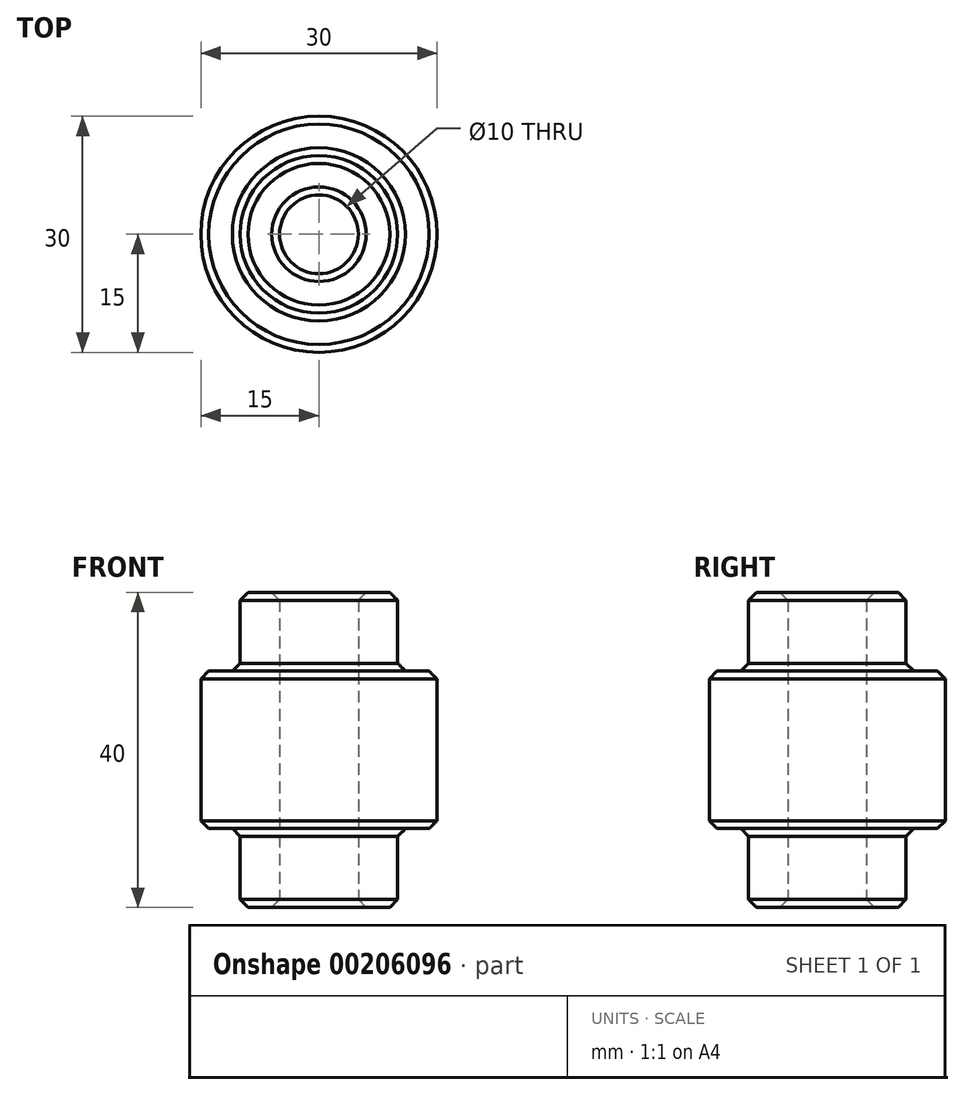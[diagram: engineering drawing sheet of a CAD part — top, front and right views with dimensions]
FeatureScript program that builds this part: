
annotation { "Feature Type Name" : "Feature", "Feature Type Description" : "" }
export const myFeature = defineFeature(function(context is Context, id is Id, definition is map)
    precondition{}
    {
        {
            var Q0;
            Q0=qCreatedBy(makeId("Top.planeOp"),FACE);
            var sketch = newSketch(context, id + "F0", { "sketchPlane" : qUnion([Q0])});
            skCircle(sketch, "E0", {"center": v(0, 0) * mm, "radius": 15 * mm});
            skSolve(sketch);
        }
        {
            var Q0;
            Q0=makeQuery(id+"F0.imprint","IMPRINT",FACE,{"disambiguationData":[TD([[makeQuery(id+"F0.imprint","IMPRINT",EDGE,{"derivedFrom":sQuery(id+"F0.wireOp",EDGE,"E0")}),1.0]])]});
            extrude(context, id + "F1", {"entities" : qUnion([Q0]), "depth" : 10 * mm, "hasSecondDirection" : true, "secondDirectionOppositeDirection" : true, "secondDirectionDepth" : 10 * mm});
        }
        {
            var Q0;
            Q0=makeQuery(id+"F1.opExtrude","CAP_FACE",FACE,{"disambiguationData":[OSD([sQuery(id+"F0.wireOp",EDGE,"E0")])],"isStart":false});
            var sketch = newSketch(context, id + "F2", { "sketchPlane" : qUnion([Q0])});
            skCircle(sketch, "E1", {"center": v(0, 0) * mm, "radius": 10 * mm});
            skSolve(sketch);
        }
        {
            var Q0;
            Q0 = qSketchRegion(id + "F2", true);
            extrude(context, id + "F3", {"entities" : qUnion([Q0]), "operationType" : NewBodyOperationType.ADD, "depth" : 10 * mm});
        }
        {
            var Q0;
            Q0=makeQuery(id+"F1.opExtrude","CAP_FACE",FACE,{"disambiguationData":[OSD([sQuery(id+"F0.wireOp",EDGE,"E0")])],"isStart":true});
            var sketch = newSketch(context, id + "F4", { "sketchPlane" : qUnion([Q0])});
            skCircle(sketch, "E2", {"center": v(0, 0) * mm, "radius": 10 * mm});
            skSolve(sketch);
        }
        {
            var Q0;
            Q0 = qSketchRegion(id + "F4", true);
            extrude(context, id + "F5", {"entities" : qUnion([Q0]), "operationType" : NewBodyOperationType.ADD, "depth" : 10 * mm});
        }
        {
            var Q0;
            Q0=makeQuery(id+"F3.opExtrude","CAP_FACE",FACE,{"disambiguationData":[OSD([sQuery(id+"F2.wireOp",EDGE,"E1")])],"isStart":false});
            var sketch = newSketch(context, id + "F6", { "sketchPlane" : qUnion([Q0])});
            skPoint(sketch, "E3", {"position": v(0, 0) * mm});
            skSolve(sketch);
        }
        {
            var Q0;
            Q0=sQuery(id+"F6.wireOp",VERTEX,"E3");
            var Q1;
            Q1=makeQuery(id+"F1.opExtrude","SWEPT_BODY",BODY,{"disambiguationData":[OSD([sQuery(id+"F0.wireOp",EDGE,"E0")])]});
            hole(context, id + "F7", {"style" : HoleStyle.SIMPLE, "endStyle" : HoleEndStyle.THROUGH, "holeDiameter" : 10 * mm, "locations" : qUnion([Q0]), "scope" : qUnion([Q1]), "isTappedThrough" : true});
        }
        {
            var Q0;
            Q0=makeQuery(id+"F3.opExtrude","CAP_FACE",FACE,{"disambiguationData":[OSD([sQuery(id+"F2.wireOp",EDGE,"E1")])],"isStart":false});
            var Q1;
            Q1=makeQuery(id+"F1.opExtrude","CAP_FACE",FACE,{"disambiguationData":[OSD([sQuery(id+"F0.wireOp",EDGE,"E0")])],"isStart":false});
            var Q2;
            Q2=makeQuery(id+"F1.opExtrude","CAP_FACE",FACE,{"disambiguationData":[OSD([sQuery(id+"F0.wireOp",EDGE,"E0")])],"isStart":true});
            var Q3;
            Q3=makeQuery(id+"F5.opExtrude","CAP_FACE",FACE,{"disambiguationData":[OSD([sQuery(id+"F4.wireOp",EDGE,"E2")])],"isStart":false});
            chamfer(context, id + "F8", {"entities" : qUnion([Q0, Q1, Q2, Q3]), "width" : 1 * mm, "tangentPropagation" : true});
        }
    });
